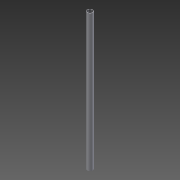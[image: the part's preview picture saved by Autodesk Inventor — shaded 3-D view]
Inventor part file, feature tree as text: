
AUTODESK INVENTOR PART (.ipt)
format: ipt  version: 2015 (Build 190159000, 159)  size: 83,456 bytes
history: native  units: mm
features: thread x2, other x1, extrude x1, shell x1, sketch x1
ambient origin geometry x8: Origin, YZ Plane, XZ Plane, XY Plane, X Axis, Y Axis, Z Axis, Center Point
bodies: Body1 (feature_tree)
feature tree (6):
  other  "Bryła1"
  extrude  "Wyciągnięcie proste1"  Depth=18.0mm
  shell  "Skorupa1"  Thickness=450.0mm
  thread  "Gwint1"
  thread  "Gwint2"
  sketch  "Szkic1"
